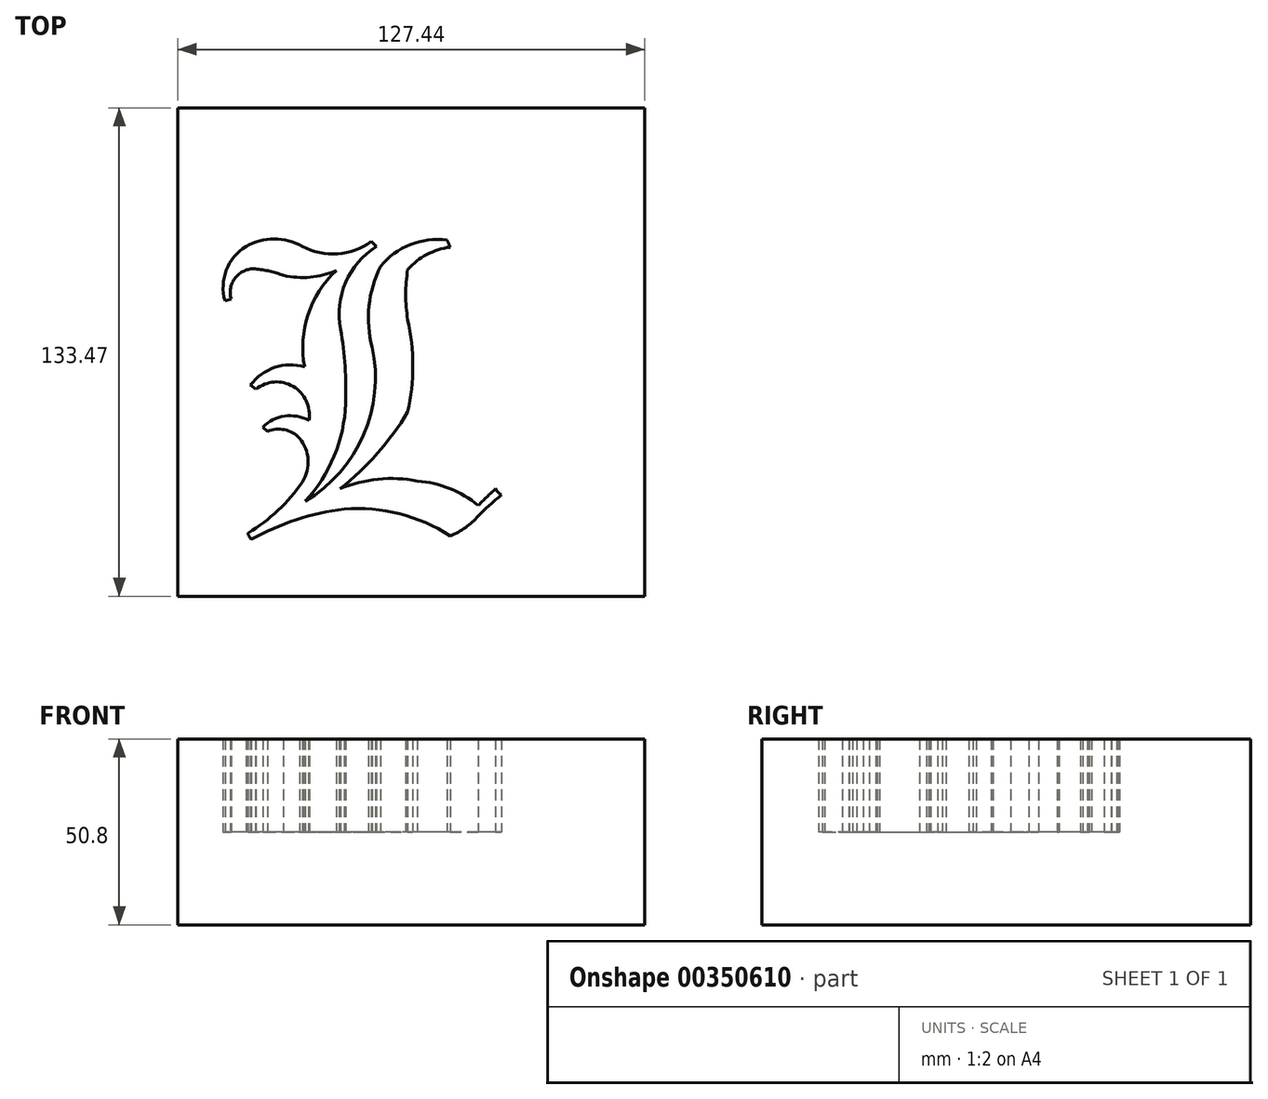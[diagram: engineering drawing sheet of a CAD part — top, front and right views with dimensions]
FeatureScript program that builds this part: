
annotation { "Feature Type Name" : "Feature", "Feature Type Description" : "" }
export const myFeature = defineFeature(function(context is Context, id is Id, definition is map)
    precondition{}
    {
        {
            var Q0;
            Q0=qCreatedBy(makeId("Top.planeOp"),FACE);
            var sketch = newSketch(context, id + "F0", { "sketchPlane" : qUnion([Q0])});
            skLineSegment(sketch, "E0.bottom", {"start": v(57.73, -63.55) * mm, "end": v(-69.71, -63.55) * mm});
            skLineSegment(sketch, "E0.top", {"start": v(57.73, 69.92) * mm, "end": v(-69.71, 69.92) * mm});
            skLineSegment(sketch, "E0.left", {"start": v(57.73, -63.55) * mm, "end": v(57.73, 69.92) * mm});
            skLineSegment(sketch, "E0.right", {"start": v(-69.71, -63.55) * mm, "end": v(-69.71, 69.92) * mm});
            skSolve(sketch);
        }
        {
            var Q0;
            Q0=makeQuery(id+"F0.imprint","IMPRINT",FACE,{"disambiguationData":[TD([[makeQuery(id+"F0.imprint","IMPRINT",EDGE,{"derivedFrom":sQuery(id+"F0.wireOp",EDGE,"E0.bottom")}),-1.0]])]});
            extrude(context, id + "F1", {"entities" : qUnion([Q0]), "depth" : 25.4 * mm});
        }
        {
            var Q0;
            Q0=makeQuery(id+"F1.opExtrude","CAP_FACE",FACE,{"disambiguationData":[OSD([sQuery(id+"F0.wireOp",EDGE,"E0.bottom"),sQuery(id+"F0.wireOp",EDGE,"E0.top"),sQuery(id+"F0.wireOp",EDGE,"E0.left"),sQuery(id+"F0.wireOp",EDGE,"E0.right")])],"isStart":false});
            var sketch = newSketch(context, id + "F2", { "sketchPlane" : qUnion([Q0])});
            skArc(sketch, "E1", {"start": v(-34.94, -37.6) * mm, "mid": v(-27.04, -25.24) * mm, "end": v(-23.9, -10.91) * mm});
            skArc(sketch, "E2", {"start": v(-23.9, -10.91) * mm, "mid": v(-24.07, -0.7) * mm, "end": v(-25.32, 9.42) * mm});
            skArc(sketch, "E3", {"start": v(-15.51, 32) * mm, "mid": v(-23.9, 22.22) * mm, "end": v(-25.32, 9.42) * mm});
            skLineSegment(sketch, "E4", {"start": v(-16.88, 33.4) * mm, "end": v(-15.51, 32) * mm});
            skArc(sketch, "E5", {"start": v(-35.73, 32.06) * mm, "mid": v(-26.11, 30.02) * mm, "end": v(-16.88, 33.4) * mm});
            skArc(sketch, "E6", {"start": v(-35.73, 32.06) * mm, "mid": v(-43.43, 34.1) * mm, "end": v(-51.12, 32.06) * mm});
            skArc(sketch, "E7", {"start": v(-51.12, 32.06) * mm, "mid": v(-56.5, 25.56) * mm, "end": v(-56.84, 17.14) * mm});
            skLineSegment(sketch, "E8", {"start": v(-56.84, 17.14) * mm, "end": v(-55.16, 17.61) * mm});
            skLineSegment(sketch, "E9", {"start": v(-55.16, 17.61) * mm, "end": v(-56.84, 17.14) * mm});
            skArc(sketch, "E10", {"start": v(-48.6, 25.91) * mm, "mid": v(-54.03, 23.46) * mm, "end": v(-55.16, 17.61) * mm});
            skArc(sketch, "E11", {"start": v(-40.88, 24.12) * mm, "mid": v(-44.68, 25.27) * mm, "end": v(-48.6, 25.91) * mm});
            skArc(sketch, "E12", {"start": v(-40.88, 24.12) * mm, "mid": v(-33.58, 23.63) * mm, "end": v(-26.49, 25.44) * mm});
            skArc(sketch, "E13", {"start": v(-26.49, 25.44) * mm, "mid": v(-34.2, 13.37) * mm, "end": v(-35.11, -0.92) * mm});
            skArc(sketch, "E14", {"start": v(-35.11, -0.92) * mm, "mid": v(-43.28, -1.06) * mm, "end": v(-49.9, -5.85) * mm});
            skLineSegment(sketch, "E15", {"start": v(-48.42, -7.02) * mm, "end": v(-49.9, -5.85) * mm});
            skArc(sketch, "E16", {"start": v(-33.96, -15.48) * mm, "mid": v(-38.24, -6.22) * mm, "end": v(-48.42, -7.02) * mm});
            skArc(sketch, "E17", {"start": v(-33.96, -15.48) * mm, "mid": v(-40.58, -14.36) * mm, "end": v(-46.56, -17.4) * mm});
            skLineSegment(sketch, "E18", {"start": v(-46.56, -17.4) * mm, "end": v(-45.3, -18.56) * mm});
            skArc(sketch, "E19", {"start": v(-36.51, -20.41) * mm, "mid": v(-40.6, -18.06) * mm, "end": v(-45.3, -18.56) * mm});
            skArc(sketch, "E20", {"start": v(-35.68, -32.34) * mm, "mid": v(-34.15, -26.24) * mm, "end": v(-36.51, -20.41) * mm});
            skArc(sketch, "E21", {"start": v(-50.57, -46.31) * mm, "mid": v(-42.38, -40.13) * mm, "end": v(-35.68, -32.34) * mm});
            skArc(sketch, "E22", {"start": v(-50.57, -46.31) * mm, "mid": v(-50.22, -47.23) * mm, "end": v(-49.65, -48.03) * mm});
            skArc(sketch, "E23", {"start": v(-24.3, -39.74) * mm, "mid": v(-37.38, -42.64) * mm, "end": v(-49.65, -48.03) * mm});
            skArc(sketch, "E24", {"start": v(4.66, -47.05) * mm, "mid": v(-9.23, -41.04) * mm, "end": v(-24.3, -39.74) * mm});
            skArc(sketch, "E25", {"start": v(4.66, -47.05) * mm, "mid": v(8.83, -44.8) * mm, "end": v(12.33, -41.6) * mm});
            skArc(sketch, "E26", {"start": v(18.64, -35.86) * mm, "mid": v(15.43, -38.66) * mm, "end": v(12.33, -41.6) * mm});
            skArc(sketch, "E27", {"start": v(17.05, -34.2) * mm, "mid": v(17.72, -35.14) * mm, "end": v(18.64, -35.86) * mm});
            skArc(sketch, "E28", {"start": v(17.05, -34.2) * mm, "mid": v(14.66, -36.43) * mm, "end": v(12.33, -38.73) * mm});
            skArc(sketch, "E29", {"start": v(12.33, -38.73) * mm, "mid": v(4.5, -34.15) * mm, "end": v(-4.32, -32.07) * mm});
            skArc(sketch, "E30", {"start": v(-4.32, -32.07) * mm, "mid": v(-15.02, -31.57) * mm, "end": v(-25.4, -34.2) * mm});
            skArc(sketch, "E31", {"start": v(-25.4, -34.2) * mm, "mid": v(-15.26, -24.53) * mm, "end": v(-6.94, -13.25) * mm});
            skArc(sketch, "E32", {"start": v(-6.94, -13.25) * mm, "mid": v(-5.57, -0.62) * mm, "end": v(-6.94, 12.02) * mm});
            skArc(sketch, "E33", {"start": v(4.66, 31.82) * mm, "mid": v(-1.71, 29.84) * mm, "end": v(-6.94, 25.7) * mm});
            skArc(sketch, "E34", {"start": v(-6.94, 25.7) * mm, "mid": v(-7.52, 18.86) * mm, "end": v(-6.94, 12.02) * mm});
            skArc(sketch, "E35", {"start": v(4.66, 31.82) * mm, "mid": v(4.24, 32.8) * mm, "end": v(3.75, 33.75) * mm});
            skArc(sketch, "E36", {"start": v(3.75, 33.75) * mm, "mid": v(-6.26, 32.53) * mm, "end": v(-14.4, 26.56) * mm});
            skArc(sketch, "E37", {"start": v(-14.4, 26.56) * mm, "mid": v(-17.52, 15.71) * mm, "end": v(-16.66, 4.45) * mm});
            skArc(sketch, "E38", {"start": v(-34.94, -37.6) * mm, "mid": v(-19.03, -19.52) * mm, "end": v(-16.66, 4.45) * mm});
            skSolve(sketch);
        }
        {
            var Q0;
            Q0=makeQuery(id+"F2.imprint","IMPRINT",FACE,{"disambiguationData":[TD([[makeQuery(id+"F2.imprint","IMPRINT",EDGE,{"derivedFrom":sQuery(id+"F2.wireOp",EDGE,"E1")}),-1.0]])]});
            extrude(context, id + "F3", {"entities" : qUnion([Q0]), "operationType" : NewBodyOperationType.ADD, "depth" : 25.4 * mm});
        }
    });
